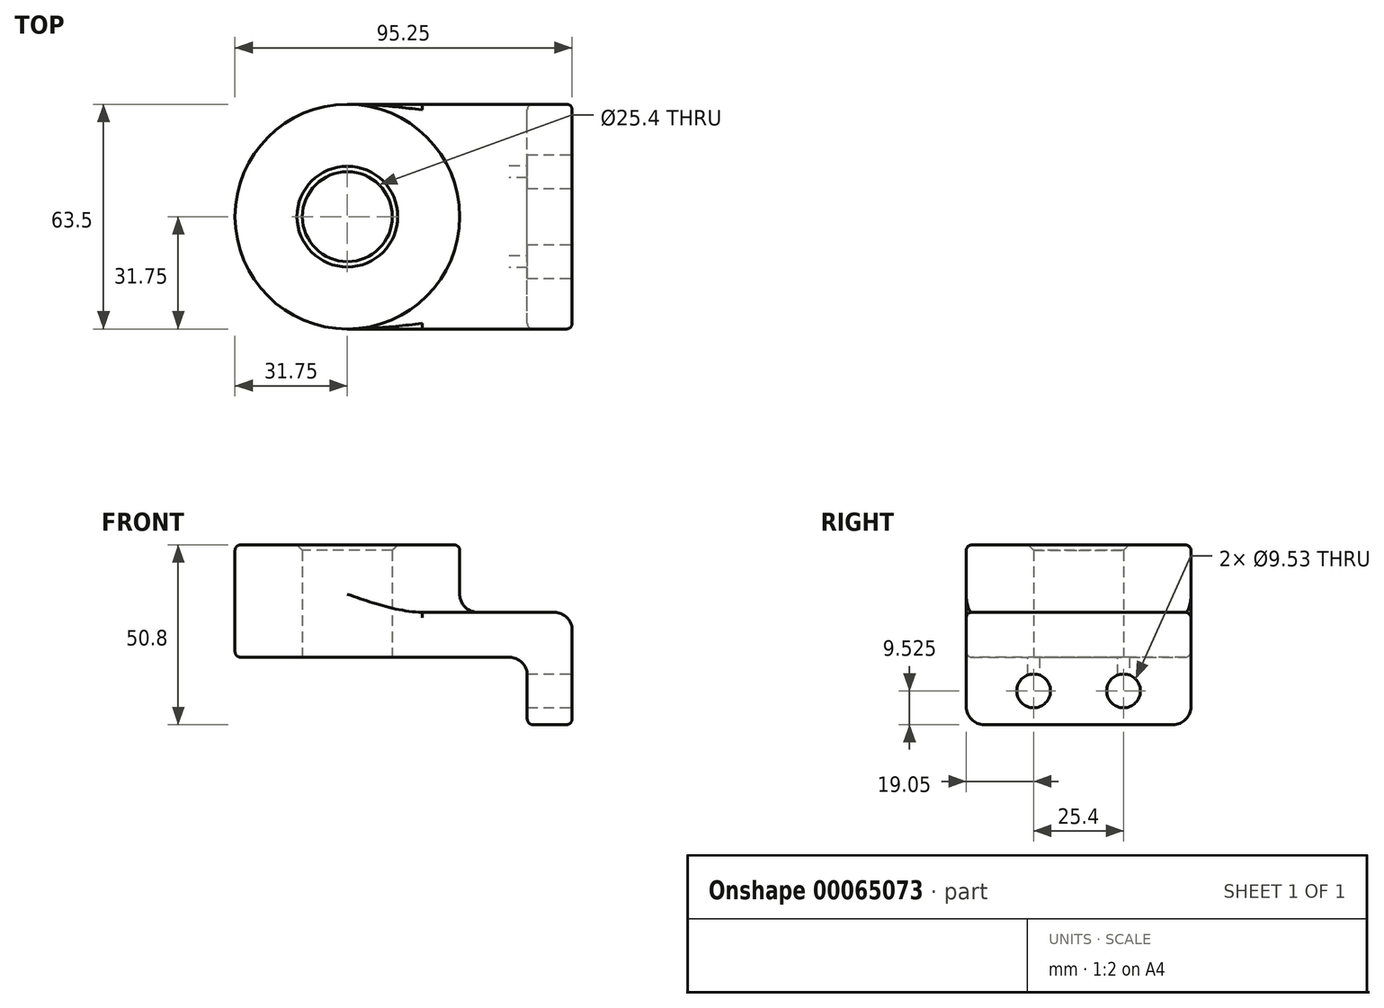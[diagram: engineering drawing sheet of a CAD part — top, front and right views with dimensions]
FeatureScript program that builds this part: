
annotation { "Feature Type Name" : "Feature", "Feature Type Description" : "" }
export const myFeature = defineFeature(function(context is Context, id is Id, definition is map)
    precondition{}
    {
        {
            var Q0;
            Q0=qCreatedBy(makeId("Top.planeOp"),FACE);
            var sketch = newSketch(context, id + "F0", { "sketchPlane" : qUnion([Q0])});
            skLineSegment(sketch, "E0.rect.bottom", {"start": v(31.75, -31.75) * mm, "end": v(-31.75, -31.75) * mm});
            skLineSegment(sketch, "E0.rect.top", {"start": v(31.75, 31.75) * mm, "end": v(-31.75, 31.75) * mm});
            skLineSegment(sketch, "E0.rect.left", {"start": v(31.75, -31.75) * mm, "end": v(31.75, 31.75) * mm});
            skLineSegment(sketch, "E0.rect.right", {"start": v(-31.75, -31.75) * mm, "end": v(-31.75, 31.75) * mm});
            skPoint(sketch, "E0.rect.middle", {"position": v(0, 0) * mm});
            skCircle(sketch, "E1", {"center": v(-31.75, 0) * mm, "radius": 31.75 * mm});
            skCircle(sketch, "E2", {"center": v(-31.75, 0) * mm, "radius": 12.7 * mm});
            skSolve(sketch);
        }
        {
            var Q0;
            {var subQ0=sQuery(id+"F0.wireOp",EDGE,"E0.rect.bottom");Q0=makeQuery(id+"F0.imprint","IMPRINT",FACE,{"disambiguationData":[TD([[makeQuery(id+"F0.imprint","IMPRINT",EDGE,{"derivedFrom":subQ0}),-1.0]])]});}
            var Q1;
            {var subQ1=sQuery(id+"F0.wireOp",EDGE,"E0.rect.right");var subQ3=sQuery(id+"F0.wireOp",EDGE,"E2");var subQ4=makeQuery(id+"F0.imprint","INTERSECT",VERTEX,{"disambiguationData":[OD(0.0)],"derivedFrom":[subQ1,subQ3]});Q1=makeQuery(id+"F0.imprint","IMPRINT",FACE,{"disambiguationData":[TD([[makeQuery(id+"F0.imprint","IMPRINT",EDGE,{"disambiguationData":[TD([[subQ4,-1.0]])],"derivedFrom":subQ3}),-1.0]])]});}
            var Q2;
            {var subQ1=sQuery(id+"F0.wireOp",EDGE,"E0.rect.right");var subQ3=sQuery(id+"F0.wireOp",EDGE,"E2");var subQ4=makeQuery(id+"F0.imprint","INTERSECT",VERTEX,{"disambiguationData":[OD(0.0)],"derivedFrom":[subQ1,subQ3]});Q2=makeQuery(id+"F0.imprint","IMPRINT",FACE,{"disambiguationData":[TD([[makeQuery(id+"F0.imprint","IMPRINT",EDGE,{"disambiguationData":[TD([[subQ4,1.0]])],"derivedFrom":subQ3}),-1.0]])]});}
            extrude(context, id + "F1", {"entities" : qUnion([Q0, Q1, Q2]), "depth" : 12.7 * mm});
        }
        {
            var Q0;
            {var subQ1=sQuery(id+"F0.wireOp",EDGE,"E0.rect.right");var subQ3=sQuery(id+"F0.wireOp",EDGE,"E2");var subQ4=makeQuery(id+"F0.imprint","INTERSECT",VERTEX,{"disambiguationData":[OD(0.0)],"derivedFrom":[subQ1,subQ3]});Q0=makeQuery(id+"F0.imprint","IMPRINT",FACE,{"disambiguationData":[TD([[makeQuery(id+"F0.imprint","IMPRINT",EDGE,{"disambiguationData":[TD([[subQ4,1.0]])],"derivedFrom":subQ3}),-1.0]])]});}
            var Q1;
            {var subQ1=sQuery(id+"F0.wireOp",EDGE,"E0.rect.right");var subQ3=sQuery(id+"F0.wireOp",EDGE,"E2");var subQ4=makeQuery(id+"F0.imprint","INTERSECT",VERTEX,{"disambiguationData":[OD(0.0)],"derivedFrom":[subQ1,subQ3]});Q1=makeQuery(id+"F0.imprint","IMPRINT",FACE,{"disambiguationData":[TD([[makeQuery(id+"F0.imprint","IMPRINT",EDGE,{"disambiguationData":[TD([[subQ4,-1.0]])],"derivedFrom":subQ3}),-1.0]])]});}
            extrude(context, id + "F2", {"entities" : qUnion([Q0, Q1]), "operationType" : NewBodyOperationType.ADD, "depth" : 31.75 * mm});
        }
        {
            var Q0;
            Q0=makeQuery(id+"F1.opExtrude","SWEPT_FACE",FACE,{"disambiguationData":[OSD([sQuery(id+"F0.wireOp",EDGE,"E0.rect.left")])]});
            var sketch = newSketch(context, id + "F3", { "sketchPlane" : qUnion([Q0])});
            skLineSegment(sketch, "E3.bottom", {"start": v(-31.75, 12.7) * mm, "end": v(31.75, 12.7) * mm});
            skLineSegment(sketch, "E3.top", {"start": v(-31.75, -19.05) * mm, "end": v(31.75, -19.05) * mm});
            skLineSegment(sketch, "E3.left", {"start": v(-31.75, 12.7) * mm, "end": v(-31.75, -19.05) * mm});
            skLineSegment(sketch, "E3.right", {"start": v(31.75, 12.7) * mm, "end": v(31.75, -19.05) * mm});
            skLineSegment(sketch, "E4", {"start": v(0, 12.7) * mm, "end": v(0, -19.05) * mm, "construction": true});
            skCircle(sketch, "E5", {"center": v(-12.7, -9.52) * mm, "radius": 4.76 * mm});
            skCircle(sketch, "E6.MirrorC", {"center": v(12.7, -9.52) * mm, "radius": 4.76 * mm});
            skSolve(sketch);
        }
        {
            var Q0;
            Q0 = qSketchRegion(id + "F3", true);
            extrude(context, id + "F4", {"entities" : qUnion([Q0]), "operationType" : NewBodyOperationType.ADD, "oppositeDirection" : true, "depth" : 12.7 * mm});
        }
        {
            var Q0;
            {var subQ0=sQuery(id+"F0.wireOp",EDGE,"E1");Q0=makeQuery(id+"F2.boolean.opBoolean","INTERSECT",EDGE,{"derivedFrom":[makeQuery(id+"F1.opExtrude","CAP_FACE",FACE,{"disambiguationData":[OSD([sQuery(id+"F0.wireOp",EDGE,"E0.rect.bottom"),sQuery(id+"F0.wireOp",EDGE,"E0.rect.top"),sQuery(id+"F0.wireOp",EDGE,"E0.rect.left"),subQ0,sQuery(id+"F0.wireOp",EDGE,"E2")])],"isStart":false}),makeQuery(id+"F2.opExtrude","SWEPT_FACE",FACE,{"disambiguationData":[OSD([subQ0])]})]});}
            var Q1;
            Q1=makeQuery(id+"F1.opExtrude","CAP_EDGE",EDGE,{"disambiguationData":[OSD([sQuery(id+"F0.wireOp",EDGE,"E0.rect.left")])],"isStart":false});
            var Q2;
            Q2=makeQuery(id+"F4.boolean.opBoolean","INTERSECT",EDGE,{"derivedFrom":[makeQuery(id+"F1.opExtrude","CAP_FACE",FACE,{"disambiguationData":[OSD([sQuery(id+"F0.wireOp",EDGE,"E0.rect.bottom"),sQuery(id+"F0.wireOp",EDGE,"E0.rect.top"),sQuery(id+"F0.wireOp",EDGE,"E0.rect.left"),sQuery(id+"F0.wireOp",EDGE,"E1"),sQuery(id+"F0.wireOp",EDGE,"E2")])],"isStart":true}),makeQuery(id+"F4.opExtrude","CAP_FACE",FACE,{"disambiguationData":[OSD([sQuery(id+"F3.wireOp",EDGE,"E3.bottom"),sQuery(id+"F3.wireOp",EDGE,"E3.top"),sQuery(id+"F3.wireOp",EDGE,"E3.left"),sQuery(id+"F3.wireOp",EDGE,"E3.right"),sQuery(id+"F3.wireOp",EDGE,"E5"),sQuery(id+"F3.wireOp",EDGE,"E6.MirrorC")])],"isStart":false})]});
            var Q3;
            Q3=makeQuery(id+"F4.opExtrude","SWEPT_EDGE",EDGE,{"disambiguationData":[OSD([sQuery(id+"F3.wireOp",EDGE,"E3.top"),sQuery(id+"F3.wireOp",EDGE,"E3.left")])]});
            var Q4;
            Q4=makeQuery(id+"F4.opExtrude","SWEPT_EDGE",EDGE,{"disambiguationData":[OSD([sQuery(id+"F3.wireOp",EDGE,"E3.top"),sQuery(id+"F3.wireOp",EDGE,"E3.right")])]});
            fillet(context, id + "F5", {"entities" : qUnion([Q0, Q1, Q2, Q3, Q4]), "radius" : 5.08 * mm, "tangentPropagation" : true, "allowEdgeOverflow" : false});
        }
        {
            var Q0;
            Q0=makeQuery(id+"F4.boolean.opBoolean","MERGE",EDGE,{"derivedFrom":[makeQuery(id+"F1.opExtrude","SWEPT_EDGE",EDGE,{"disambiguationData":[OSD([sQuery(id+"F0.wireOp",EDGE,"E0.rect.bottom"),sQuery(id+"F0.wireOp",EDGE,"E0.rect.left")])]}),makeQuery(id+"F4.opExtrude","CAP_EDGE",EDGE,{"disambiguationData":[OSD([sQuery(id+"F3.wireOp",EDGE,"E3.left")])],"isStart":true})]});
            var Q1;
            {var subQ0=sQuery(id+"F3.wireOp",EDGE,"E3.left");var subQ1=sQuery(id+"F0.wireOp",EDGE,"E0.rect.bottom");Q1=makeQuery(id+"F5.opFillet","BLEND_EDGE",EDGE,{"blendedFrom":[makeQuery(id+"F4.boolean.opBoolean","INTERSECT",EDGE,{"derivedFrom":[makeQuery(id+"F1.opExtrude","CAP_FACE",FACE,{"disambiguationData":[OSD([subQ1,sQuery(id+"F0.wireOp",EDGE,"E0.rect.top"),sQuery(id+"F0.wireOp",EDGE,"E0.rect.left"),sQuery(id+"F0.wireOp",EDGE,"E1"),sQuery(id+"F0.wireOp",EDGE,"E2")])],"isStart":true}),makeQuery(id+"F4.opExtrude","CAP_FACE",FACE,{"disambiguationData":[OSD([sQuery(id+"F3.wireOp",EDGE,"E3.bottom"),sQuery(id+"F3.wireOp",EDGE,"E3.top"),subQ0,sQuery(id+"F3.wireOp",EDGE,"E3.right"),sQuery(id+"F3.wireOp",EDGE,"E5"),sQuery(id+"F3.wireOp",EDGE,"E6.MirrorC")])],"isStart":false})]}),makeQuery(id+"F4.boolean.opBoolean","MERGE",FACE,{"derivedFrom":[makeQuery(id+"F1.opExtrude","SWEPT_FACE",FACE,{"disambiguationData":[OSD([subQ1])]}),makeQuery(id+"F4.opExtrude","SWEPT_FACE",FACE,{"disambiguationData":[OSD([subQ0])]})]})],"blendedInto":[makeQuery(id+"F4.boolean.opBoolean","MERGE",FACE,{"derivedFrom":[makeQuery(id+"F1.opExtrude","SWEPT_FACE",FACE,{"disambiguationData":[OSD([subQ1])]}),makeQuery(id+"F4.opExtrude","SWEPT_FACE",FACE,{"disambiguationData":[OSD([subQ0])]})]})]});}
            var Q2;
            Q2=makeQuery(id+"F2.opExtrude","CAP_EDGE",EDGE,{"disambiguationData":[OSD([sQuery(id+"F0.wireOp",EDGE,"E1")])],"isStart":false});
            fillet(context, id + "F6", {"entities" : qUnion([Q0, Q1, Q2]), "radius" : 1.59 * mm, "tangentPropagation" : true, "allowEdgeOverflow" : false});
        }
        {
            var Q0;
            Q0=makeQuery(id+"F2.opExtrude","CAP_EDGE",EDGE,{"disambiguationData":[OSD([sQuery(id+"F0.wireOp",EDGE,"E2")])],"isStart":false});
            chamfer(context, id + "F7", {"entities" : qUnion([Q0]), "width" : 1.52 * mm, "tangentPropagation" : true});
        }
    });
